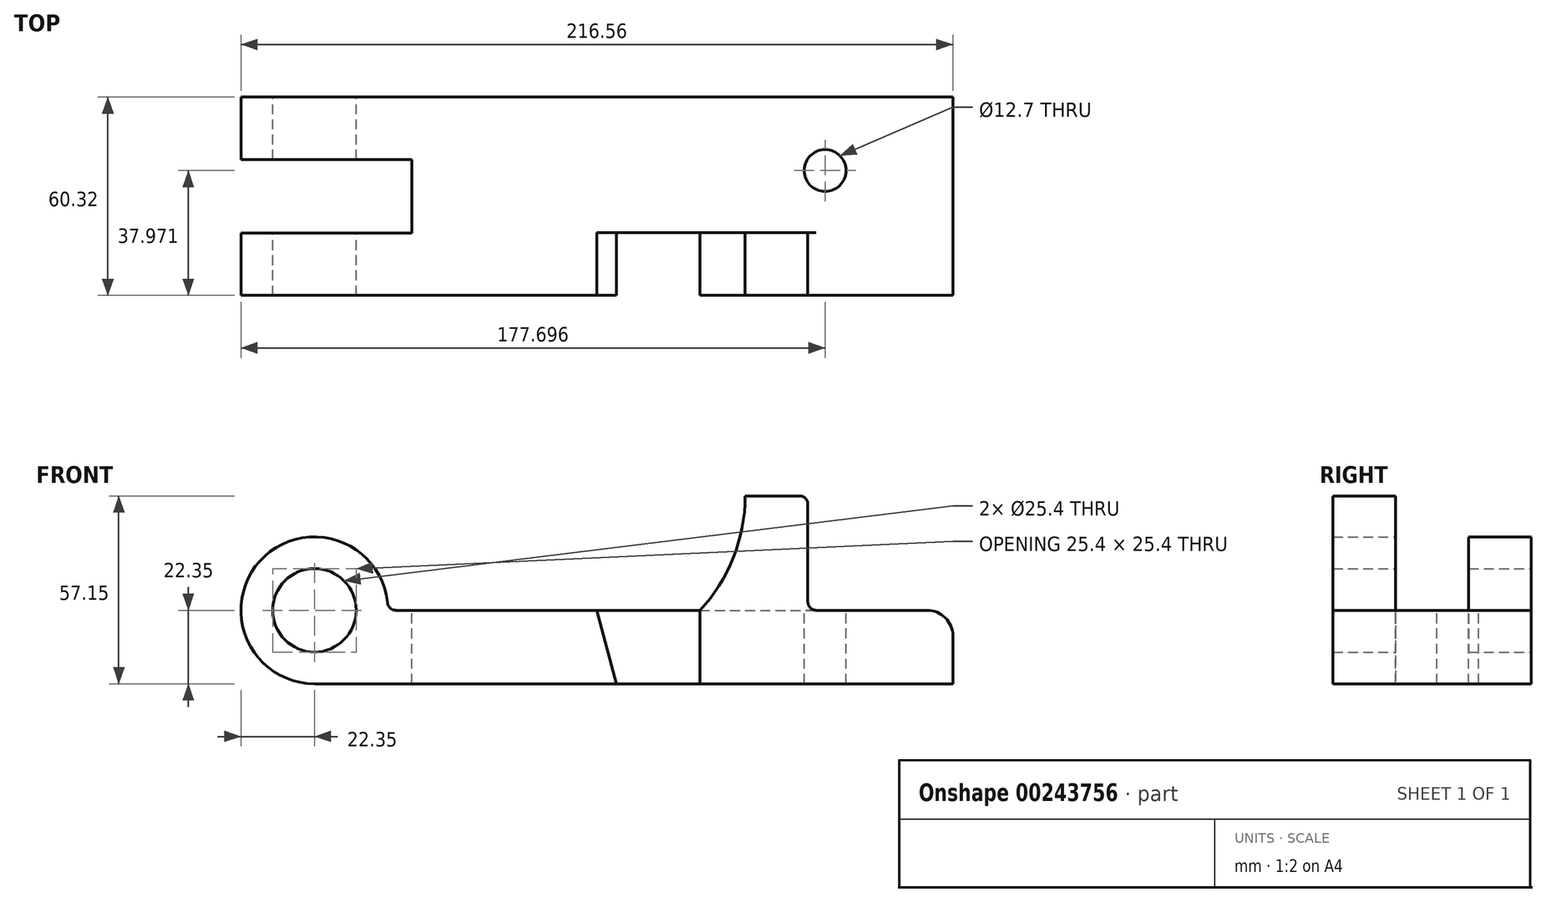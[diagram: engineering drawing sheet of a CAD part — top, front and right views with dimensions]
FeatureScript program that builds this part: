
annotation { "Feature Type Name" : "Feature", "Feature Type Description" : "" }
export const myFeature = defineFeature(function(context is Context, id is Id, definition is map)
    precondition{}
    {
        {
            var Q0;
            Q0=qCreatedBy(makeId("Front.planeOp"),FACE);
            var sketch = newSketch(context, id + "F0", { "sketchPlane" : qUnion([Q0])});
            skCircle(sketch, "E0", {"center": v(0, 0) * mm, "radius": 12.7 * mm});
            skArc(sketch, "E1", {"start": v(22.35, 0) * mm, "mid": v(-15.8, 15.8) * mm, "end": v(0, -22.35) * mm});
            skLineSegment(sketch, "E2", {"start": v(22.35, 0) * mm, "end": v(194.2, 0) * mm});
            skLineSegment(sketch, "E3", {"start": v(194.2, 0) * mm, "end": v(194.2, -22.35) * mm});
            skLineSegment(sketch, "E4", {"start": v(194.2, -22.35) * mm, "end": v(0, -22.35) * mm});
            skLineSegment(sketch, "E5", {"start": v(85.85, 0) * mm, "end": v(91.85, -22.35) * mm});
            skLineSegment(sketch, "E6", {"start": v(117.25, 0) * mm, "end": v(117.25, -22.35) * mm});
            skLineSegment(sketch, "E7", {"start": v(150.09, 0) * mm, "end": v(150.09, 34.8) * mm});
            skLineSegment(sketch, "E8", {"start": v(150.09, 34.8) * mm, "end": v(131.04, 34.8) * mm});
            skArc(sketch, "E9", {"start": v(117.25, 0) * mm, "mid": v(127.46, 16.08) * mm, "end": v(131.04, 34.8) * mm});
            skSolve(sketch);
        }
        {
            var Q0;
            Q0=makeQuery(id+"F0.imprint","IMPRINT",FACE,{"disambiguationData":[TD([[makeQuery(id+"F0.imprint","IMPRINT",EDGE,{"derivedFrom":sQuery(id+"F0.wireOp",EDGE,"E0")}),-1.0]])]});
            var Q1;
            {var subQ1=sQuery(id+"F0.wireOp",EDGE,"E3");Q1=makeQuery(id+"F0.imprint","IMPRINT",FACE,{"disambiguationData":[TD([[makeQuery(id+"F0.imprint","IMPRINT",EDGE,{"derivedFrom":subQ1}),-1.0]])]});}
            extrude(context, id + "F1", {"entities" : qUnion([Q0, Q1]), "endBound" : BoundingType.SYMMETRIC, "depth" : 60.32 * mm});
        }
        {
            var Q0;
            Q0=makeQuery(id+"F1.opExtrude","SWEPT_EDGE",EDGE,{"disambiguationData":[OSD([sQuery(id+"F0.wireOp",EDGE,"E2"),sQuery(id+"F0.wireOp",EDGE,"E3")])]});
            fillet(context, id + "F2", {"entities" : qUnion([Q0]), "radius" : 7.87 * mm, "tangentPropagation" : true, "allowEdgeOverflow" : false});
        }
        {
            var Q0;
            Q0=makeQuery(id+"F1.opExtrude","SWEPT_EDGE",EDGE,{"disambiguationData":[OSD([sQuery(id+"F0.wireOp",EDGE,"E1"),sQuery(id+"F0.wireOp",EDGE,"E2")])]});
            fillet(context, id + "F3", {"entities" : qUnion([Q0]), "radius" : 2.54 * mm, "tangentPropagation" : true, "allowEdgeOverflow" : false});
        }
        {
            var Q0;
            {var subQ0=sQuery(id+"F0.wireOp",EDGE,"E5");Q0=makeQuery(id+"F0.imprint","IMPRINT",FACE,{"disambiguationData":[TD([[makeQuery(id+"F0.imprint","IMPRINT",EDGE,{"derivedFrom":subQ0}),1.0]])]});}
            var Q1;
            {var subQ2=sQuery(id+"F0.wireOp",EDGE,"E7");Q1=makeQuery(id+"F0.imprint","IMPRINT",FACE,{"disambiguationData":[TD([[makeQuery(id+"F0.imprint","IMPRINT",EDGE,{"derivedFrom":subQ2}),1.0]])]});}
            extrude(context, id + "F4", {"entities" : qUnion([Q0, Q1]), "endBound" : BoundingType.SYMMETRIC, "oppositeDirection" : true, "depth" : 60.32 * mm});
        }
        {
            var Q0;
            Q0=makeQuery(id+"F4.opExtrude","CAP_FACE",FACE,{"disambiguationData":[OSD([sQuery(id+"F0.wireOp",EDGE,"E2"),sQuery(id+"F0.wireOp",EDGE,"E4"),sQuery(id+"F0.wireOp",EDGE,"E5"),sQuery(id+"F0.wireOp",EDGE,"E6")])],"isStart":true});
            extrude(context, id + "F5", {"entities" : qUnion([Q0]), "operationType" : NewBodyOperationType.REMOVE, "oppositeDirection" : true, "depth" : 19.05 * mm});
        }
        {
            var Q0;
            Q0=makeQuery(id+"F4.opExtrude","CAP_FACE",FACE,{"disambiguationData":[OSD([sQuery(id+"F0.wireOp",EDGE,"E2"),sQuery(id+"F0.wireOp",EDGE,"E7"),sQuery(id+"F0.wireOp",EDGE,"E8"),sQuery(id+"F0.wireOp",EDGE,"E9")])],"isStart":false});
            extrude(context, id + "F6", {"entities" : qUnion([Q0]), "operationType" : NewBodyOperationType.REMOVE, "oppositeDirection" : true, "depth" : 41.27 * mm});
        }
        {
            var Q0;
            Q0=makeQuery(id+"F1.opExtrude","SWEPT_BODY",BODY,{"disambiguationData":[OSD([sQuery(id+"F0.wireOp",EDGE,"E2"),sQuery(id+"F0.wireOp",EDGE,"E3"),sQuery(id+"F0.wireOp",EDGE,"E4"),sQuery(id+"F0.wireOp",EDGE,"E6")])]});
            var Q1;
            Q1=makeQuery(id+"F4.opExtrude","SWEPT_BODY",BODY,{"disambiguationData":[OSD([sQuery(id+"F0.wireOp",EDGE,"E2"),sQuery(id+"F0.wireOp",EDGE,"E4"),sQuery(id+"F0.wireOp",EDGE,"E5"),sQuery(id+"F0.wireOp",EDGE,"E6")])]});
            var Q2;
            Q2=makeQuery(id+"F1.opExtrude","SWEPT_BODY",BODY,{"disambiguationData":[OSD([sQuery(id+"F0.wireOp",EDGE,"E0"),sQuery(id+"F0.wireOp",EDGE,"E1"),sQuery(id+"F0.wireOp",EDGE,"E2"),sQuery(id+"F0.wireOp",EDGE,"E4"),sQuery(id+"F0.wireOp",EDGE,"E5")])]});
            var Q3;
            Q3=makeQuery(id+"F4.opExtrude","SWEPT_BODY",BODY,{"disambiguationData":[OSD([sQuery(id+"F0.wireOp",EDGE,"E2"),sQuery(id+"F0.wireOp",EDGE,"E7"),sQuery(id+"F0.wireOp",EDGE,"E8"),sQuery(id+"F0.wireOp",EDGE,"E9")])]});
            booleanBodies(context, id + "F7", {"operationType" : BooleanOperationType.UNION, "tools" : qUnion([Q0, Q1, Q2, Q3])});
        }
        {
            var Q0;
            Q0=makeQuery(id+"F4.opExtrude","SWEPT_EDGE",EDGE,{"disambiguationData":[OSD([sQuery(id+"F0.wireOp",EDGE,"E7"),sQuery(id+"F0.wireOp",EDGE,"E8")])]});
            var Q1;
            Q1=makeQuery(id+"F4.opExtrude","SWEPT_EDGE",EDGE,{"disambiguationData":[OSD([sQuery(id+"F0.wireOp",EDGE,"E2"),sQuery(id+"F0.wireOp",EDGE,"E7")])]});
            fillet(context, id + "F8", {"entities" : qUnion([Q0, Q1]), "radius" : 2.54 * mm, "tangentPropagation" : true, "allowEdgeOverflow" : false});
        }
        {
            var Q0;
            {var subQ0=sQuery(id+"F0.wireOp",EDGE,"E2");var subQ1=makeQuery(id+"F0.imprint","INTERSECT",VERTEX,{"derivedFrom":[subQ0,sQuery(id+"F0.wireOp",EDGE,"E5")]});var subQ3=makeQuery(id+"F0.imprint","INTERSECT",VERTEX,{"derivedFrom":[subQ0,sQuery(id+"F0.wireOp",EDGE,"E7")]});Q0=makeQuery(id+"F7.opBoolean","MERGE",FACE,{"derivedFrom":[makeQuery(id+"F1.opExtrude","SWEPT_FACE",FACE,{"disambiguationData":[OSD([subQ0]),TDD([makeQuery(id+"F0.imprint","IMPRINT",EDGE,{"disambiguationData":[TD([[subQ3,1.0]])],"derivedFrom":subQ0}),makeQuery(id+"F0.imprint","IMPRINT",EDGE,{"disambiguationData":[TD([[makeQuery(id+"F0.imprint","INTERSECT",VERTEX,{"derivedFrom":[subQ0,sQuery(id+"F0.wireOp",EDGE,"E3")]}),1.0]])],"derivedFrom":subQ0})])]}),makeQuery(id+"F1.opExtrude","SWEPT_FACE",FACE,{"disambiguationData":[OSD([subQ0]),TDD([makeQuery(id+"F0.imprint","IMPRINT",EDGE,{"disambiguationData":[TD([[makeQuery(id+"F0.imprint","INTERSECT",VERTEX,{"derivedFrom":[sQuery(id+"F0.wireOp",EDGE,"E1"),subQ0]}),-1.0]])],"derivedFrom":subQ0})])]}),makeQuery(id+"F4.opExtrude","SWEPT_FACE",FACE,{"disambiguationData":[OSD([subQ0]),TDD([makeQuery(id+"F0.imprint","IMPRINT",EDGE,{"disambiguationData":[TD([[subQ1,-1.0]])],"derivedFrom":subQ0})])]})]});}
            var sketch = newSketch(context, id + "F9", { "sketchPlane" : qUnion([Q0])});
            skCircle(sketch, "E10", {"center": v(155.35, 7.81) * mm, "radius": 6.35 * mm});
            skSolve(sketch);
        }
        {
            var Q0;
            Q0 = qSketchRegion(id + "F9", true);
            extrude(context, id + "F10", {"entities" : qUnion([Q0]), "operationType" : NewBodyOperationType.REMOVE, "endBound" : BoundingType.THROUGH_ALL, "oppositeDirection" : true, "depth" : 76.2 * mm});
        }
        {
            var Q0;
            Q0=qCreatedBy(makeId("Top.planeOp"),FACE);
            var sketch = newSketch(context, id + "F11", { "sketchPlane" : qUnion([Q0])});
            skLineSegment(sketch, "E11.bottom", {"start": v(-29.61, 11.16) * mm, "end": v(29.59, 11.16) * mm});
            skLineSegment(sketch, "E11.top", {"start": v(-29.61, -11.16) * mm, "end": v(29.59, -11.16) * mm});
            skLineSegment(sketch, "E11.left", {"start": v(-29.61, 11.16) * mm, "end": v(-29.61, -11.16) * mm});
            skLineSegment(sketch, "E11.right", {"start": v(29.59, 11.16) * mm, "end": v(29.59, -11.16) * mm});
            skSolve(sketch);
        }
        {
            var Q0;
            Q0=makeQuery(id+"F11.imprint","IMPRINT",FACE,{"disambiguationData":[TD([[makeQuery(id+"F11.imprint","IMPRINT",EDGE,{"derivedFrom":sQuery(id+"F11.wireOp",EDGE,"E11.bottom")}),-1.0]])]});
            extrude(context, id + "F12", {"entities" : qUnion([Q0]), "operationType" : NewBodyOperationType.REMOVE, "endBound" : BoundingType.THROUGH_ALL, "depth" : 88.65 * mm});
        }
        {
            var Q0;
            Q0=makeQuery(id+"F11.imprint","IMPRINT",FACE,{"disambiguationData":[TD([[makeQuery(id+"F11.imprint","IMPRINT",EDGE,{"derivedFrom":sQuery(id+"F11.wireOp",EDGE,"E11.bottom")}),-1.0]])]});
            extrude(context, id + "F13", {"entities" : qUnion([Q0]), "operationType" : NewBodyOperationType.REMOVE, "oppositeDirection" : true, "depth" : 45.2 * mm});
        }
    });
